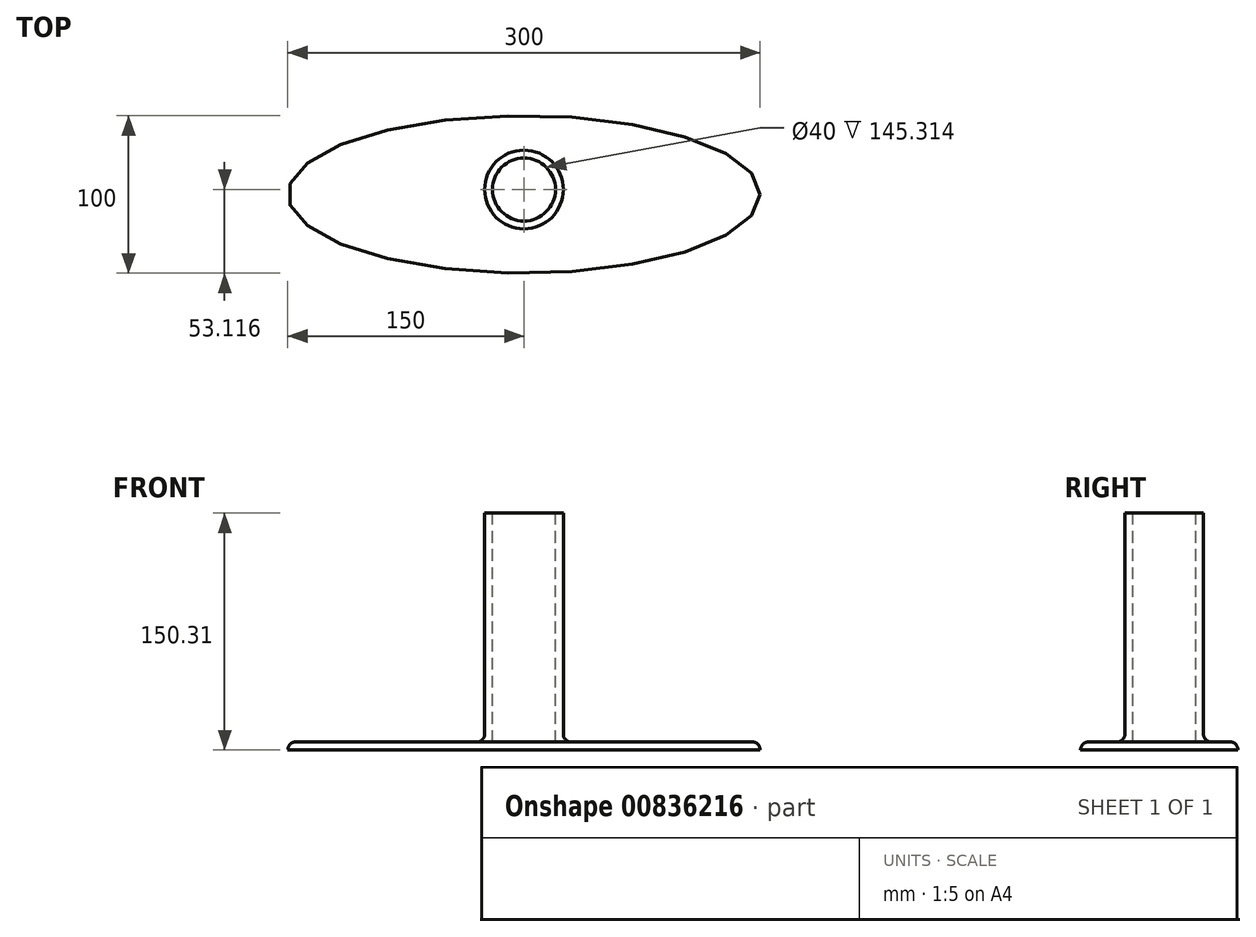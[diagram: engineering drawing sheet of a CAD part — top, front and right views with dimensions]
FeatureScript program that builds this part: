
annotation { "Feature Type Name" : "Feature", "Feature Type Description" : "" }
export const myFeature = defineFeature(function(context is Context, id is Id, definition is map)
    precondition{}
    {
        {
            var Q0;
            Q0=qCreatedBy(makeId("Top.planeOp"),FACE);
            var sketch = newSketch(context, id + "F0", { "sketchPlane" : qUnion([Q0])});
            skEllipse(sketch, "E0", {"center": v(0, 0) * mm, "majorRadius": 150 * mm, "minorRadius": 50 * mm, "majorAxis": v(1, 0)});
            skSolve(sketch);
        }
        {
            var Q0;
            Q0=qCreatedBy(makeId("Top.planeOp"),FACE);
            cPlane(context, id + "F1", {"entities" : qUnion([Q0]), "cplaneType" : CPlaneType.OFFSET, "offset" : 150 * mm, "width" : 150 * mm, "height" : 150 * mm});
        }
        {
            var Q0;
            Q0=qCreatedBy(id+"F1.planeOp",FACE);
            var sketch = newSketch(context, id + "F2", { "sketchPlane" : qUnion([Q0])});
            skCircle(sketch, "E1", {"center": v(0, 3.12) * mm, "radius": 25 * mm});
            skCircle(sketch, "E2.0", {"center": v(0, 3.12) * mm, "radius": 20 * mm});
            skSolve(sketch);
        }
        {
            var Q0;
            Q0=qCreatedBy(makeId("Front.planeOp"),FACE);
            var sketch = newSketch(context, id + "F3", { "sketchPlane" : qUnion([Q0])});
            skLineSegment(sketch, "E3", {"start": v(0, 150.31) * mm, "end": v(0, 0) * mm});
            skSolve(sketch);
        }
        {
            var Q0;
            Q0=makeQuery(id+"F2.imprint","IMPRINT",FACE,{"disambiguationData":[TD([[makeQuery(id+"F2.imprint","IMPRINT",EDGE,{"derivedFrom":sQuery(id+"F2.wireOp",EDGE,"E1")}),1.0]])]});
            var Q1;
            Q1=sQuery(id+"F3.wireOp",EDGE,"E3");
            sweep(context, id + "F4", {"profiles" : qUnion([Q0]), "path" : qUnion([Q1])});
        }
        {
            var Q0;
            Q0=makeQuery(id+"F0.imprint","IMPRINT",FACE,{"disambiguationData":[TD([[makeQuery(id+"F0.imprint","IMPRINT",EDGE,{"derivedFrom":sQuery(id+"F0.wireOp",EDGE,"E0")}),1.0]])]});
            extrude(context, id + "F5", {"entities" : qUnion([Q0]), "operationType" : NewBodyOperationType.ADD, "depth" : 5 * mm, "offsetDistance" : 25 * mm});
        }
        {
            var Q0;
            {var subQ0=sQuery(id+"F0.wireOp",EDGE,"E0");Q0=makeQuery(id+"F5.boolean.opBoolean","SPLIT",FACE,{"disambiguationData":[TD([makeQuery(id+"F5.opExtrude","SWEPT_FACE",FACE,{"disambiguationData":[OSD([subQ0])]})])],"derivedFrom":makeQuery(id+"F5.opExtrude","CAP_FACE",FACE,{"disambiguationData":[OSD([subQ0])],"isStart":false})});}
            fillet(context, id + "F6", {"entities" : qUnion([Q0]), "radius" : 5 * mm, "tangentPropagation" : true, "allowEdgeOverflow" : false});
        }
    });
